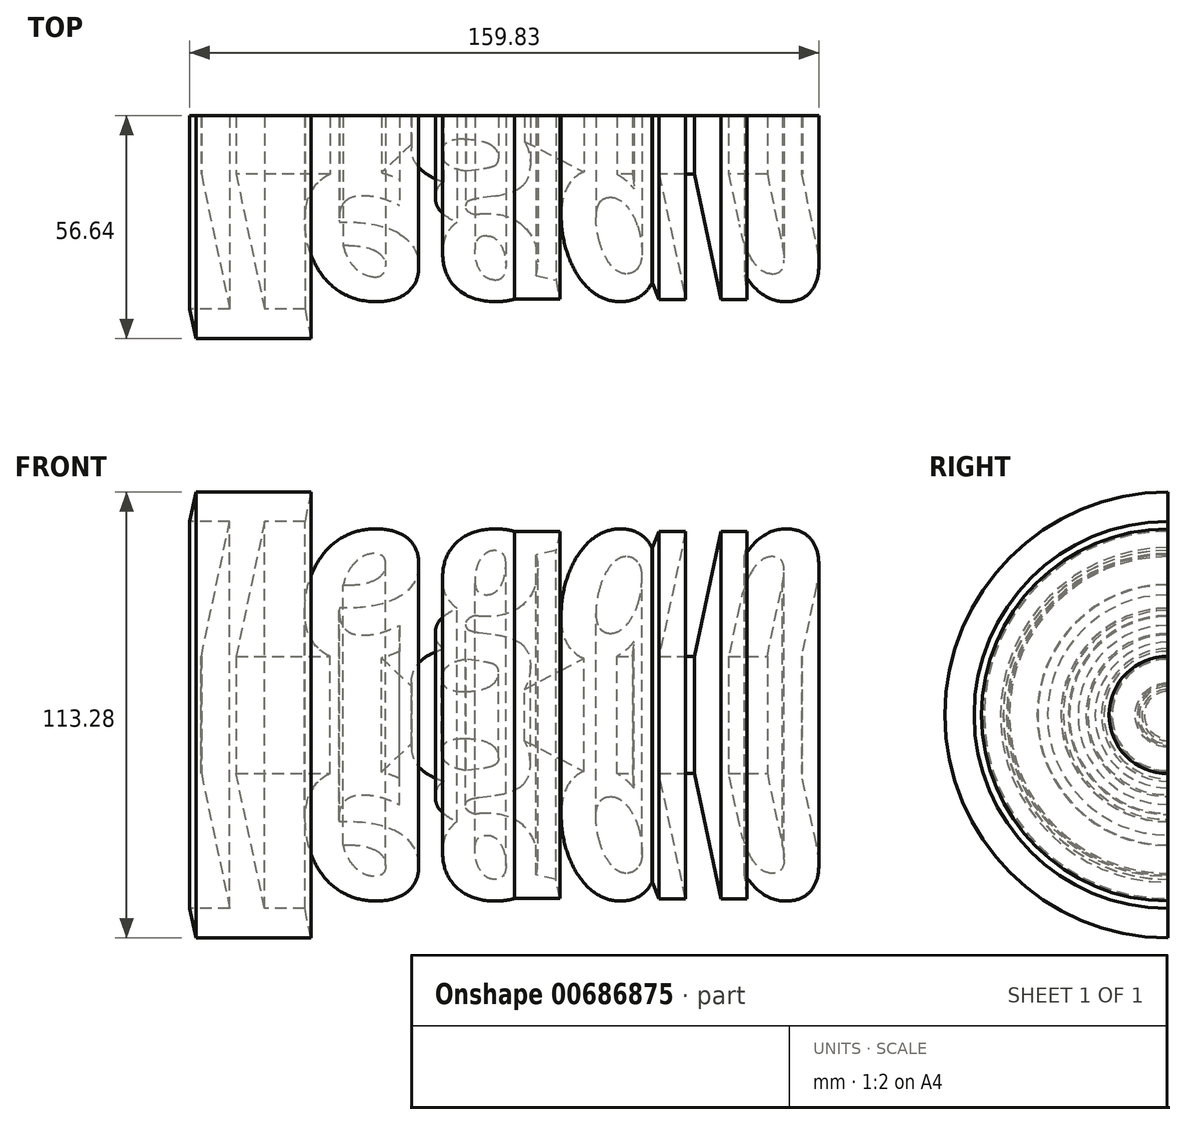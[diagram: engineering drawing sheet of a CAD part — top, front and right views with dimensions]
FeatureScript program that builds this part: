
annotation { "Feature Type Name" : "Feature", "Feature Type Description" : "" }
export const myFeature = defineFeature(function(context is Context, id is Id, definition is map)
    precondition{}
    {
        {
            var Q0;
            Q0=qCreatedBy(makeId("Front.planeOp"),FACE);
            var sketch = newSketch(context, id + "F0", { "sketchPlane" : qUnion([Q0])});
            skText(sketch, "E0", { "text": "Tegan", "fontName": "OpenSans-BoldItalic.ttf"});
            skLineSegment(sketch, "E1.bottom", {"start": v(-63.83, 14.29) * mm, "end": v(89.27, 14.29) * mm, "construction": true});
            skLineSegment(sketch, "E1.top", {"start": v(-63.83, 0) * mm, "end": v(89.27, 0) * mm});
            skLineSegment(sketch, "E1.left", {"start": v(-63.83, 14.29) * mm, "end": v(-63.83, 0) * mm});
            skLineSegment(sketch, "E1.right", {"start": v(89.27, 14.29) * mm, "end": v(89.27, 0) * mm});
            skLineSegment(sketch, "E2", {"start": v(-15.7, 14.29) * mm, "end": v(-3.07, 0) * mm});
            skLineSegment(sketch, "E3", {"start": v(-3.07, 0) * mm, "end": v(9.56, 0) * mm, "construction": true});
            skLineSegment(sketch, "E4", {"start": v(9.56, 0) * mm, "end": v(29.41, 14.29) * mm});
            const initialGuessF0  = {"E0": [-0.07114, 0.01429, 1, 0, 0.04271]};
            skSetInitialGuess(sketch, initialGuessF0);
            skSolve(sketch);
        }
        {
            var Q0;
            Q0 = qSketchRegion(id + "F0", true);
            var Q1;
            Q1=sQuery(id+"F0.wireOp",EDGE,"E1.top");
            revolve(context, id + "F1", {"entities" : qUnion([Q0]), "axis" : qUnion([Q1]), "revolveType" : RevolveType.ONE_DIRECTION, "angle" : 180 * degree});
        }
        {
            var Q0;
            Q0=qCreatedBy(makeId("Front.planeOp"),FACE);
            var sketch = newSketch(context, id + "F2", { "sketchPlane" : qUnion([Q0])});
            skLineSegment(sketch, "E5", {"start": v(89.45, 0) * mm, "end": v(-63.35, 0) * mm});
            skLineSegment(sketch, "E6", {"start": v(-63.35, 14.89) * mm, "end": v(-17.93, 14.89) * mm});
            skLineSegment(sketch, "E7", {"start": v(-17.93, 14.89) * mm, "end": v(-6.5, 4.06) * mm});
            skLineSegment(sketch, "E8", {"start": v(-6.5, 4.06) * mm, "end": v(13.95, 4.06) * mm});
            skLineSegment(sketch, "E9", {"start": v(13.95, 4.06) * mm, "end": v(35, 14.89) * mm});
            skLineSegment(sketch, "E10", {"start": v(35, 14.89) * mm, "end": v(89.45, 14.89) * mm});
            skLineSegment(sketch, "E11", {"start": v(89.45, 14.89) * mm, "end": v(89.45, 0) * mm});
            skLineSegment(sketch, "E12", {"start": v(-63.35, 14.89) * mm, "end": v(-63.35, 0) * mm});
            skSolve(sketch);
        }
        {
            var Q0;
            Q0 = qSketchRegion(id + "F2", true);
            var Q1;
            Q1=sQuery(id+"F2.wireOp",EDGE,"E5");
            revolve(context, id + "F3", {"operationType" : NewBodyOperationType.ADD, "entities" : qUnion([Q0]), "axis" : qUnion([Q1]), "revolveType" : RevolveType.ONE_DIRECTION, "oppositeDirection" : true, "angle" : 180 * degree});
        }
    });
